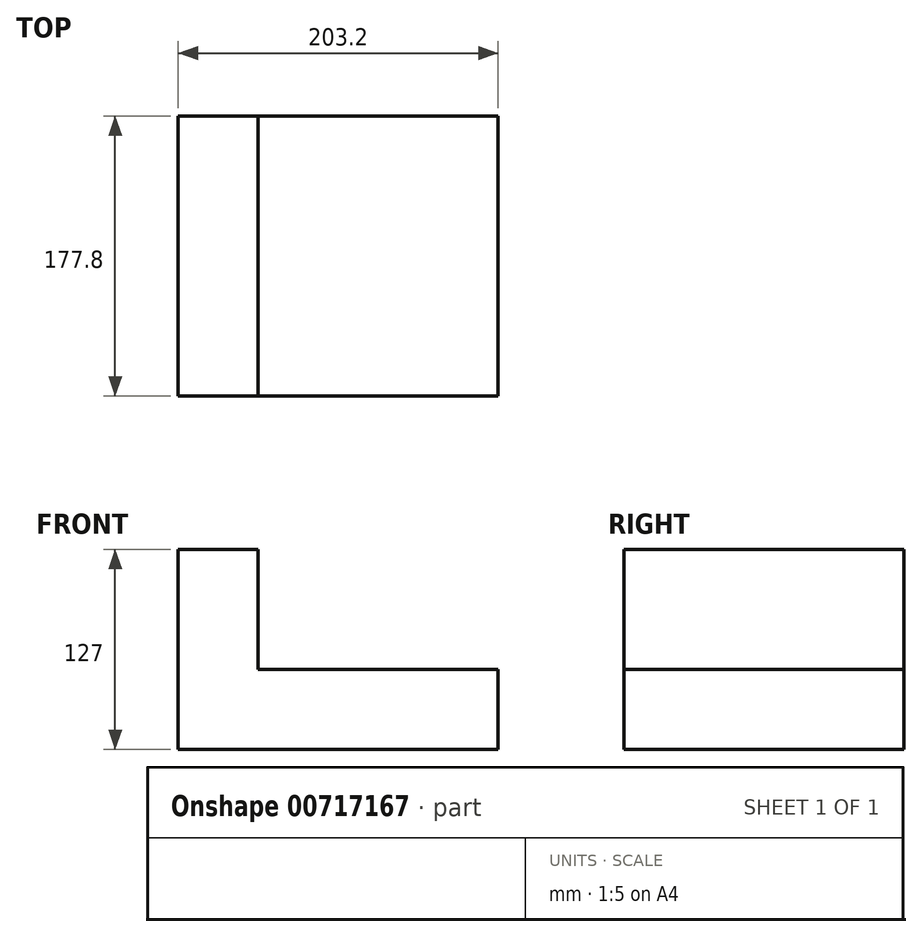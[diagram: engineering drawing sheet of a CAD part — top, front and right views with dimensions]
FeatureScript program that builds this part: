
annotation { "Feature Type Name" : "Feature", "Feature Type Description" : "" }
export const myFeature = defineFeature(function(context is Context, id is Id, definition is map)
    precondition{}
    {
        {
            var Q0;
            Q0=qCreatedBy(makeId("Front.planeOp"),FACE);
            var sketch = newSketch(context, id + "F0", { "sketchPlane" : qUnion([Q0])});
            skLineSegment(sketch, "E0", {"start": v(-57.56, -50.8) * mm, "end": v(145.64, -50.8) * mm});
            skLineSegment(sketch, "E1", {"start": v(145.64, -50.8) * mm, "end": v(145.64, 0) * mm});
            skLineSegment(sketch, "E2", {"start": v(145.64, 0) * mm, "end": v(-6.76, 0) * mm});
            skLineSegment(sketch, "E3", {"start": v(-6.76, 0) * mm, "end": v(-6.76, 76.2) * mm});
            skLineSegment(sketch, "E4", {"start": v(-6.76, 76.2) * mm, "end": v(-57.56, 76.2) * mm});
            skLineSegment(sketch, "E5", {"start": v(-57.56, 76.2) * mm, "end": v(-57.56, -50.8) * mm});
            skSolve(sketch);
        }
        {
            var Q0;
            Q0=makeQuery(id+"F0.imprint","IMPRINT",FACE,{"disambiguationData":[TD([[makeQuery(id+"F0.imprint","IMPRINT",EDGE,{"derivedFrom":sQuery(id+"F0.wireOp",EDGE,"E0")}),1.0]])]});
            extrude(context, id + "F1", {"entities" : qUnion([Q0]), "depth" : 177.8 * mm, "offsetDistance" : 25.4 * mm});
        }
    });
